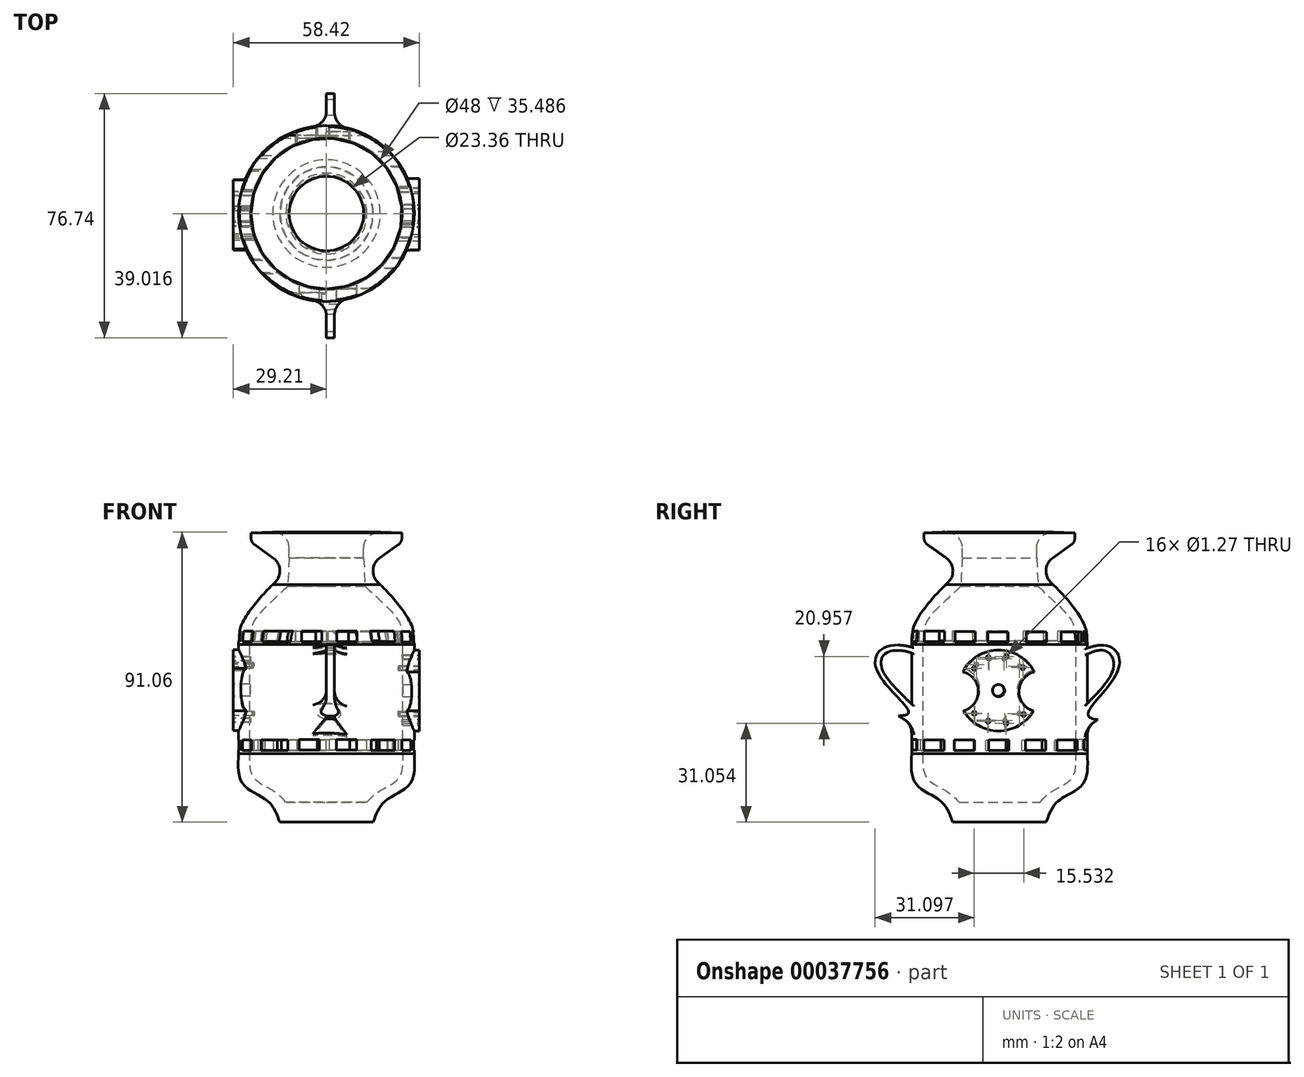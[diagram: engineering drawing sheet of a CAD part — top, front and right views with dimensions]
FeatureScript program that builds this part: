
annotation { "Feature Type Name" : "Feature", "Feature Type Description" : "" }
export const myFeature = defineFeature(function(context is Context, id is Id, definition is map)
    precondition{}
    {
        {
            var Q0;
            Q0=qCreatedBy(makeId("Right.planeOp"),FACE);
            var sketch = newSketch(context, id + "F0", { "sketchPlane" : qUnion([Q0])});
            skLineSegment(sketch, "E0", {"start": v(14.52, -21.43) * mm, "end": v(-0.17, -21.43) * mm});
            skLineSegment(sketch, "E1", {"start": v(-0.17, -21.43) * mm, "end": v(-0.17, -15.13) * mm});
            skLineSegment(sketch, "E2", {"start": v(11.5, 64.55) * mm, "end": v(11.5, 61.54) * mm});
            skLineSegment(sketch, "E3", {"start": v(-0.17, 79.99) * mm, "end": v(-0.17, -32.45) * mm, "construction": true});
            skPoint(sketch, "E4.visualSharp", {"position": v(11.5, 75.56) * mm});
            skArc(sketch, "E4.filletArc", {"start": v(16.78, 69.62) * mm, "mid": v(13.06, 68.2) * mm, "end": v(11.5, 64.55) * mm});
            skPoint(sketch, "E5.visualSharp", {"position": v(12.68, 59.63) * mm});
            skArc(sketch, "E5.filletArc", {"start": v(16.58, 61.54) * mm, "mid": v(14.44, 57.33) * mm, "end": v(16.7, 53.18) * mm});
            skPoint(sketch, "E6.visualSharp", {"position": v(11.5, 61.05) * mm});
            skArc(sketch, "E6.filletArc", {"start": v(11.5, 61.54) * mm, "mid": v(11.62, 60.46) * mm, "end": v(11.96, 59.43) * mm});
            skFitSpline(sketch, "E7", {"points": [v(16.7, 53.18) * mm, v(22.1, 47.25) * mm, v(26.83, 39.53) * mm, v(27.4, 34.38) * mm], "startDerivative": vector(15.54, -15.8) * mm, "endDerivative": vector(0.96, -17.5) * mm});
            skLineSegment(sketch, "E8", {"start": v(11.5, 61.54) * mm, "end": v(11.96, 52.7) * mm});
            skFitSpline(sketch, "E9", {"points": [v(11.96, 52.7) * mm, v(22.54, 41.67) * mm, v(23.82, 35.52) * mm], "startDerivative": vector(17.32, -18.3) * mm, "endDerivative": vector(3.54, -17.15) * mm});
            skLineSegment(sketch, "E10", {"start": v(27.4, 34.38) * mm, "end": v(27.4, 0.03) * mm});
            skLineSegment(sketch, "E11", {"start": v(23.82, 35.52) * mm, "end": v(23.82, 0.03) * mm});
            skFitSpline(sketch, "E12", {"points": [v(14.52, -21.43) * mm, v(18.24, -14.85) * mm, v(25.97, -9.55) * mm, v(27.4, 0.03) * mm], "startDerivative": vector(8.27, 23.62) * mm, "endDerivative": vector(-1.61, 31.15) * mm});
            skFitSpline(sketch, "E13", {"points": [v(23.82, 0.03) * mm, v(23.82, -3.69) * mm, v(22.25, -7.98) * mm, v(16.24, -11.84) * mm, v(12.52, -15.13) * mm], "startDerivative": vector(0.76, -16.8) * mm, "endDerivative": vector(-12.82, -13.7) * mm});
            skLineSegment(sketch, "E14", {"start": v(-0.17, -15.13) * mm, "end": v(12.52, -15.13) * mm});
            skLineSegment(sketch, "E15", {"start": v(16.78, 69.62) * mm, "end": v(23.47, 69.37) * mm});
            skLineSegment(sketch, "E16", {"start": v(16.58, 61.54) * mm, "end": v(22.41, 65.67) * mm});
            skLineSegment(sketch, "E17", {"start": v(23.48, 67.77) * mm, "end": v(23.47, 69.37) * mm});
            skPoint(sketch, "E18.visualSharp", {"position": v(23.5, 66.44) * mm});
            skArc(sketch, "E18.filletArc", {"start": v(22.41, 65.67) * mm, "mid": v(23.2, 66.59) * mm, "end": v(23.48, 67.77) * mm});
            skSolve(sketch);
        }
        {
            var Q0;
            Q0=makeQuery(id+"F0.imprint","IMPRINT",FACE,{"disambiguationData":[TD([[makeQuery(id+"F0.imprint","IMPRINT",EDGE,{"derivedFrom":sQuery(id+"F0.wireOp",EDGE,"E0")}),-1.0]])]});
            var Q1;
            Q1=sQuery(id+"F0.wireOp",EDGE,"E3");
            revolve(context, id + "F1", {"entities" : qUnion([Q0]), "axis" : qUnion([Q1]), "revolveType" : RevolveType.FULL});
        }
        {
            var Q0;
            Q0=qCreatedBy(makeId("Right.planeOp"),FACE);
            var sketch = newSketch(context, id + "F2", { "sketchPlane" : qUnion([Q0])});
            skLineSegment(sketch, "E19.bottom", {"start": v(-25.33, 38.52) * mm, "end": v(-18.98, 38.52) * mm});
            skLineSegment(sketch, "E19.top", {"start": v(-25.33, 35.22) * mm, "end": v(-18.98, 35.22) * mm});
            skLineSegment(sketch, "E19.left", {"start": v(-25.33, 38.52) * mm, "end": v(-25.33, 35.22) * mm});
            skLineSegment(sketch, "E19.right", {"start": v(-18.98, 38.52) * mm, "end": v(-18.98, 35.22) * mm});
            skLineSegment(sketch, "E20.bottom", {"start": v(-14.87, 38.52) * mm, "end": v(-8.52, 38.52) * mm});
            skLineSegment(sketch, "E20.top", {"start": v(-14.87, 35.22) * mm, "end": v(-8.52, 35.22) * mm});
            skLineSegment(sketch, "E20.left", {"start": v(-14.87, 38.52) * mm, "end": v(-14.87, 35.22) * mm});
            skLineSegment(sketch, "E20.right", {"start": v(-8.52, 38.52) * mm, "end": v(-8.52, 35.22) * mm});
            skLineSegment(sketch, "E21.bottom", {"start": v(-4.15, 38.52) * mm, "end": v(2.2, 38.52) * mm});
            skLineSegment(sketch, "E21.top", {"start": v(-4.15, 35.22) * mm, "end": v(2.2, 35.22) * mm});
            skLineSegment(sketch, "E21.left", {"start": v(-4.15, 38.52) * mm, "end": v(-4.15, 35.22) * mm});
            skLineSegment(sketch, "E21.right", {"start": v(2.2, 38.52) * mm, "end": v(2.2, 35.22) * mm});
            skLineSegment(sketch, "E22.bottom", {"start": v(7.37, 38.52) * mm, "end": v(13.72, 38.52) * mm});
            skLineSegment(sketch, "E22.top", {"start": v(7.37, 35.22) * mm, "end": v(13.72, 35.22) * mm});
            skLineSegment(sketch, "E22.left", {"start": v(7.37, 38.52) * mm, "end": v(7.37, 35.22) * mm});
            skLineSegment(sketch, "E22.right", {"start": v(13.72, 38.52) * mm, "end": v(13.72, 35.22) * mm});
            skLineSegment(sketch, "E23.bottom", {"start": v(18.1, 38.52) * mm, "end": v(24.45, 38.52) * mm});
            skLineSegment(sketch, "E23.top", {"start": v(18.1, 35.22) * mm, "end": v(24.45, 35.22) * mm});
            skLineSegment(sketch, "E23.left", {"start": v(18.1, 38.52) * mm, "end": v(18.1, 35.22) * mm});
            skLineSegment(sketch, "E23.right", {"start": v(24.45, 38.52) * mm, "end": v(24.45, 35.22) * mm});
            skLineSegment(sketch, "E24.bottom", {"start": v(-14.47, 4.36) * mm, "end": v(-8.12, 4.36) * mm});
            skLineSegment(sketch, "E24.top", {"start": v(-14.47, 1.06) * mm, "end": v(-8.12, 1.06) * mm});
            skLineSegment(sketch, "E24.left", {"start": v(-14.47, 4.36) * mm, "end": v(-14.47, 1.06) * mm});
            skLineSegment(sketch, "E24.right", {"start": v(-8.12, 4.36) * mm, "end": v(-8.12, 1.06) * mm});
            skLineSegment(sketch, "E25.bottom", {"start": v(-4.4, 4.36) * mm, "end": v(1.94, 4.36) * mm});
            skLineSegment(sketch, "E25.top", {"start": v(-4.4, 1.06) * mm, "end": v(1.94, 1.06) * mm});
            skLineSegment(sketch, "E25.left", {"start": v(-4.4, 4.36) * mm, "end": v(-4.4, 1.06) * mm});
            skLineSegment(sketch, "E25.right", {"start": v(1.94, 4.36) * mm, "end": v(1.94, 1.06) * mm});
            skLineSegment(sketch, "E26.bottom", {"start": v(6.85, 4.36) * mm, "end": v(13.2, 4.36) * mm});
            skLineSegment(sketch, "E26.top", {"start": v(6.85, 1.06) * mm, "end": v(13.2, 1.06) * mm});
            skLineSegment(sketch, "E26.left", {"start": v(6.85, 4.36) * mm, "end": v(6.85, 1.06) * mm});
            skLineSegment(sketch, "E26.right", {"start": v(13.2, 4.36) * mm, "end": v(13.2, 1.06) * mm});
            skLineSegment(sketch, "E27.bottom", {"start": v(17.18, 4.36) * mm, "end": v(23.53, 4.36) * mm});
            skLineSegment(sketch, "E27.top", {"start": v(17.18, 1.06) * mm, "end": v(23.53, 1.06) * mm});
            skLineSegment(sketch, "E27.left", {"start": v(17.18, 4.36) * mm, "end": v(17.18, 1.06) * mm});
            skLineSegment(sketch, "E27.right", {"start": v(23.53, 4.36) * mm, "end": v(23.53, 1.06) * mm});
            skLineSegment(sketch, "E28.bottom", {"start": v(-24.93, 4.36) * mm, "end": v(-18.58, 4.36) * mm});
            skLineSegment(sketch, "E28.top", {"start": v(-24.93, 1.06) * mm, "end": v(-18.58, 1.06) * mm});
            skLineSegment(sketch, "E28.left", {"start": v(-24.93, 4.36) * mm, "end": v(-24.93, 1.06) * mm});
            skLineSegment(sketch, "E28.right", {"start": v(-18.58, 4.36) * mm, "end": v(-18.58, 1.06) * mm});
            skSolve(sketch);
        }
        {
            var Q0;
            Q0 = qSketchRegion(id + "F2", true);
            extrude(context, id + "F3", {"entities" : qUnion([Q0]), "operationType" : NewBodyOperationType.REMOVE, "endBound" : BoundingType.THROUGH_ALL, "oppositeDirection" : true, "depth" : 43.48 * mm});
        }
        {
            var Q0;
            Q0=qCreatedBy(makeId("Right.planeOp"),FACE);
            var sketch = newSketch(context, id + "F4", { "sketchPlane" : qUnion([Q0])});
            skLineSegment(sketch, "E29.bottom", {"start": v(-23.72, 38.57) * mm, "end": v(-17.37, 38.57) * mm});
            skLineSegment(sketch, "E29.top", {"start": v(-23.72, 35.27) * mm, "end": v(-17.37, 35.27) * mm});
            skLineSegment(sketch, "E29.left", {"start": v(-23.72, 38.57) * mm, "end": v(-23.72, 35.27) * mm});
            skLineSegment(sketch, "E29.right", {"start": v(-17.37, 38.57) * mm, "end": v(-17.37, 35.27) * mm});
            skLineSegment(sketch, "E30.bottom", {"start": v(-14.11, 38.4) * mm, "end": v(-7.76, 38.4) * mm});
            skLineSegment(sketch, "E30.top", {"start": v(-14.11, 35.1) * mm, "end": v(-7.76, 35.1) * mm});
            skLineSegment(sketch, "E30.left", {"start": v(-14.11, 38.4) * mm, "end": v(-14.11, 35.1) * mm});
            skLineSegment(sketch, "E30.right", {"start": v(-7.76, 38.4) * mm, "end": v(-7.76, 35.1) * mm});
            skLineSegment(sketch, "E31.bottom", {"start": v(-3.76, 38.22) * mm, "end": v(2.59, 38.22) * mm});
            skLineSegment(sketch, "E31.top", {"start": v(-3.76, 34.92) * mm, "end": v(2.59, 34.92) * mm});
            skLineSegment(sketch, "E31.left", {"start": v(-3.76, 38.22) * mm, "end": v(-3.76, 34.92) * mm});
            skLineSegment(sketch, "E31.right", {"start": v(2.59, 38.22) * mm, "end": v(2.59, 34.92) * mm});
            skLineSegment(sketch, "E32.bottom", {"start": v(8.27, 38.22) * mm, "end": v(14.62, 38.22) * mm});
            skLineSegment(sketch, "E32.top", {"start": v(8.27, 34.92) * mm, "end": v(14.62, 34.92) * mm});
            skLineSegment(sketch, "E32.left", {"start": v(8.27, 38.22) * mm, "end": v(8.27, 34.92) * mm});
            skLineSegment(sketch, "E32.right", {"start": v(14.62, 38.22) * mm, "end": v(14.62, 34.92) * mm});
            skLineSegment(sketch, "E33.bottom", {"start": v(19.24, 38.22) * mm, "end": v(25.59, 38.22) * mm});
            skLineSegment(sketch, "E33.top", {"start": v(19.24, 34.92) * mm, "end": v(25.59, 34.92) * mm});
            skLineSegment(sketch, "E33.left", {"start": v(19.24, 38.22) * mm, "end": v(19.24, 34.92) * mm});
            skLineSegment(sketch, "E33.right", {"start": v(25.59, 38.22) * mm, "end": v(25.59, 34.92) * mm});
            skLineSegment(sketch, "E34.bottom", {"start": v(-23.88, 4.36) * mm, "end": v(-17.53, 4.36) * mm});
            skLineSegment(sketch, "E34.top", {"start": v(-23.88, 1.06) * mm, "end": v(-17.53, 1.06) * mm});
            skLineSegment(sketch, "E34.left", {"start": v(-23.88, 4.36) * mm, "end": v(-23.88, 1.06) * mm});
            skLineSegment(sketch, "E34.right", {"start": v(-17.53, 4.36) * mm, "end": v(-17.53, 1.06) * mm});
            skLineSegment(sketch, "E35.bottom", {"start": v(-14.34, 4.36) * mm, "end": v(-8, 4.36) * mm});
            skLineSegment(sketch, "E35.top", {"start": v(-14.34, 1.06) * mm, "end": v(-8, 1.06) * mm});
            skLineSegment(sketch, "E35.left", {"start": v(-14.34, 4.36) * mm, "end": v(-14.34, 1.06) * mm});
            skLineSegment(sketch, "E35.right", {"start": v(-8, 4.36) * mm, "end": v(-8, 1.06) * mm});
            skLineSegment(sketch, "E36.bottom", {"start": v(-3.62, 4.36) * mm, "end": v(2.73, 4.36) * mm});
            skLineSegment(sketch, "E36.top", {"start": v(-3.62, 1.06) * mm, "end": v(2.73, 1.06) * mm});
            skLineSegment(sketch, "E36.left", {"start": v(-3.62, 4.36) * mm, "end": v(-3.62, 1.06) * mm});
            skLineSegment(sketch, "E36.right", {"start": v(2.73, 4.36) * mm, "end": v(2.73, 1.06) * mm});
            skLineSegment(sketch, "E37.bottom", {"start": v(8.04, 4.36) * mm, "end": v(14.39, 4.36) * mm});
            skLineSegment(sketch, "E37.top", {"start": v(8.04, 1.06) * mm, "end": v(14.39, 1.06) * mm});
            skLineSegment(sketch, "E37.left", {"start": v(8.04, 4.36) * mm, "end": v(8.04, 1.06) * mm});
            skLineSegment(sketch, "E37.right", {"start": v(14.39, 4.36) * mm, "end": v(14.39, 1.06) * mm});
            skLineSegment(sketch, "E38.bottom", {"start": v(17.97, 4.36) * mm, "end": v(24.32, 4.36) * mm});
            skLineSegment(sketch, "E38.top", {"start": v(17.97, 1.06) * mm, "end": v(24.32, 1.06) * mm});
            skLineSegment(sketch, "E38.left", {"start": v(17.97, 4.36) * mm, "end": v(17.97, 1.06) * mm});
            skLineSegment(sketch, "E38.right", {"start": v(24.32, 4.36) * mm, "end": v(24.32, 1.06) * mm});
            skSolve(sketch);
        }
        {
            var Q0;
            Q0 = qSketchRegion(id + "F4", true);
            extrude(context, id + "F5", {"entities" : qUnion([Q0]), "operationType" : NewBodyOperationType.REMOVE, "depth" : 76.34 * mm});
        }
        {
            var Q0;
            Q0=qCreatedBy(makeId("Front.planeOp"),FACE);
            var sketch = newSketch(context, id + "F6", { "sketchPlane" : qUnion([Q0])});
            skLineSegment(sketch, "E39.bottom", {"start": v(-7.82, 38.52) * mm, "end": v(-1.47, 38.52) * mm});
            skLineSegment(sketch, "E39.top", {"start": v(-7.82, 35.22) * mm, "end": v(-1.47, 35.22) * mm});
            skLineSegment(sketch, "E39.left", {"start": v(-7.82, 38.52) * mm, "end": v(-7.82, 35.22) * mm});
            skLineSegment(sketch, "E39.right", {"start": v(-1.47, 38.52) * mm, "end": v(-1.47, 35.22) * mm});
            skLineSegment(sketch, "E40.bottom", {"start": v(3.21, 38.52) * mm, "end": v(9.56, 38.52) * mm});
            skLineSegment(sketch, "E40.top", {"start": v(3.21, 35.22) * mm, "end": v(9.56, 35.22) * mm});
            skLineSegment(sketch, "E40.left", {"start": v(3.21, 38.52) * mm, "end": v(3.21, 35.22) * mm});
            skLineSegment(sketch, "E40.right", {"start": v(9.56, 38.52) * mm, "end": v(9.56, 35.22) * mm});
            skLineSegment(sketch, "E41.bottom", {"start": v(-8.6, 4.5) * mm, "end": v(-2.26, 4.5) * mm});
            skLineSegment(sketch, "E41.top", {"start": v(-8.6, 1.2) * mm, "end": v(-2.26, 1.2) * mm});
            skLineSegment(sketch, "E41.left", {"start": v(-8.6, 4.5) * mm, "end": v(-8.6, 1.2) * mm});
            skLineSegment(sketch, "E41.right", {"start": v(-2.26, 4.5) * mm, "end": v(-2.26, 1.2) * mm});
            skLineSegment(sketch, "E42.bottom", {"start": v(3.18, 4.5) * mm, "end": v(9.53, 4.5) * mm});
            skLineSegment(sketch, "E42.top", {"start": v(3.18, 1.2) * mm, "end": v(9.53, 1.2) * mm});
            skLineSegment(sketch, "E42.left", {"start": v(3.18, 4.5) * mm, "end": v(3.18, 1.2) * mm});
            skLineSegment(sketch, "E42.right", {"start": v(9.53, 4.5) * mm, "end": v(9.53, 1.2) * mm});
            skSolve(sketch);
        }
        {
            var Q0;
            Q0=makeQuery(id+"F6.imprint","IMPRINT",FACE,{"disambiguationData":[TD([[makeQuery(id+"F6.imprint","IMPRINT",EDGE,{"derivedFrom":sQuery(id+"F6.wireOp",EDGE,"E39.bottom")}),-1.0]])]});
            var Q1;
            Q1=makeQuery(id+"F6.imprint","IMPRINT",FACE,{"disambiguationData":[TD([[makeQuery(id+"F6.imprint","IMPRINT",EDGE,{"derivedFrom":sQuery(id+"F6.wireOp",EDGE,"E40.bottom")}),-1.0]])]});
            extrude(context, id + "F7", {"entities" : qUnion([Q0, Q1]), "operationType" : NewBodyOperationType.REMOVE, "depth" : 59.65 * mm});
        }
        {
            var Q0;
            Q0=qCreatedBy(makeId("Front.planeOp"),FACE);
            var sketch = newSketch(context, id + "F8", { "sketchPlane" : qUnion([Q0])});
            skLineSegment(sketch, "E43.bottom", {"start": v(6.93, 38.44) * mm, "end": v(0.58, 38.44) * mm});
            skLineSegment(sketch, "E43.top", {"start": v(6.93, 35.14) * mm, "end": v(0.58, 35.14) * mm});
            skLineSegment(sketch, "E43.left", {"start": v(6.93, 38.44) * mm, "end": v(6.93, 35.14) * mm});
            skLineSegment(sketch, "E43.right", {"start": v(0.58, 38.44) * mm, "end": v(0.58, 35.14) * mm});
            skLineSegment(sketch, "E44.bottom", {"start": v(-3.3, 38.44) * mm, "end": v(-9.66, 38.44) * mm});
            skLineSegment(sketch, "E44.top", {"start": v(-3.3, 35.14) * mm, "end": v(-9.66, 35.14) * mm});
            skLineSegment(sketch, "E44.left", {"start": v(-3.3, 38.44) * mm, "end": v(-3.3, 35.14) * mm});
            skLineSegment(sketch, "E44.right", {"start": v(-9.66, 38.44) * mm, "end": v(-9.66, 35.14) * mm});
            skLineSegment(sketch, "E45.bottom", {"start": v(-2.79, 4.5) * mm, "end": v(-9.14, 4.5) * mm});
            skLineSegment(sketch, "E45.top", {"start": v(-2.79, 1.19) * mm, "end": v(-9.14, 1.19) * mm});
            skLineSegment(sketch, "E45.left", {"start": v(-2.79, 4.5) * mm, "end": v(-2.79, 1.19) * mm});
            skLineSegment(sketch, "E45.right", {"start": v(-9.14, 4.5) * mm, "end": v(-9.14, 1.19) * mm});
            skLineSegment(sketch, "E46.bottom", {"start": v(7.28, 4.5) * mm, "end": v(0.93, 4.5) * mm});
            skLineSegment(sketch, "E46.top", {"start": v(7.28, 1.19) * mm, "end": v(0.93, 1.19) * mm});
            skLineSegment(sketch, "E46.left", {"start": v(7.28, 4.5) * mm, "end": v(7.28, 1.19) * mm});
            skLineSegment(sketch, "E46.right", {"start": v(0.93, 4.5) * mm, "end": v(0.93, 1.19) * mm});
            skSolve(sketch);
        }
        {
            var Q0;
            Q0 = qSketchRegion(id + "F8", true);
            extrude(context, id + "F9", {"entities" : qUnion([Q0]), "operationType" : NewBodyOperationType.REMOVE, "oppositeDirection" : true, "depth" : 65.15 * mm});
        }
        {
            var Q0;
            Q0 = qSketchRegion(id + "F6", true);
            extrude(context, id + "F10", {"entities" : qUnion([Q0]), "operationType" : NewBodyOperationType.REMOVE, "depth" : 87.53 * mm});
        }
        {
            var Q0;
            Q0=qCreatedBy(makeId("Right.planeOp"),FACE);
            var sketch = newSketch(context, id + "F11", { "sketchPlane" : qUnion([Q0])});
            skArc(sketch, "E47", {"start": v(10.82, 25.72) * mm, "mid": v(-0.42, 32.54) * mm, "end": v(-11.67, 25.72) * mm});
            skArc(sketch, "E48", {"start": v(10.82, 25.72) * mm, "mid": v(5.95, 19.71) * mm, "end": v(10.53, 13.49) * mm});
            skArc(sketch, "E49", {"start": v(-11.4, 13.53) * mm, "mid": v(-6.8, 19.73) * mm, "end": v(-11.67, 25.72) * mm});
            skArc(sketch, "E50.trimOffspring", {"start": v(-11.4, 13.53) * mm, "mid": v(-0.45, 7.19) * mm, "end": v(10.53, 13.49) * mm});
            skSolve(sketch);
        }
        {
            var Q0;
            Q0 = qSketchRegion(id + "F11", true);
            extrude(context, id + "F12", {"entities" : qUnion([Q0]), "operationType" : NewBodyOperationType.ADD, "depth" : 29.2 * mm, "hasSecondDirection" : true, "secondDirectionOppositeDirection" : false, "secondDirectionDepth" : 25.17 * mm});
        }
        {
            var Q0;
            Q0=qCreatedBy(makeId("Right.planeOp"),FACE);
            var sketch = newSketch(context, id + "F13", { "sketchPlane" : qUnion([Q0])});
            skArc(sketch, "E51", {"start": v(-11.62, 13.57) * mm, "mid": v(-0.77, 7.3) * mm, "end": v(10.18, 13.38) * mm});
            skArc(sketch, "E52", {"start": v(-11.62, 13.57) * mm, "mid": v(-6.43, 20.12) * mm, "end": v(-11.33, 26.88) * mm});
            skArc(sketch, "E53", {"start": v(10.42, 26.2) * mm, "mid": v(5.46, 19.88) * mm, "end": v(10.18, 13.38) * mm});
            skArc(sketch, "E54.trimOffspring", {"start": v(10.42, 26.2) * mm, "mid": v(-0.26, 32.69) * mm, "end": v(-11.33, 26.88) * mm});
            skSolve(sketch);
        }
        {
            var Q0;
            Q0 = qSketchRegion(id + "F13", true);
            extrude(context, id + "F14", {"entities" : qUnion([Q0]), "operationType" : NewBodyOperationType.ADD, "oppositeDirection" : true, "depth" : 29.2 * mm, "hasSecondDirection" : true, "secondDirectionOppositeDirection" : true, "secondDirectionDepth" : 25.17 * mm});
        }
        {
            var Q0;
            Q0=makeQuery(id+"F14.opExtrude","CAP_FACE",FACE,{"disambiguationData":[OSD([sQuery(id+"F13.wireOp",EDGE,"E51"),sQuery(id+"F13.wireOp",EDGE,"E52"),sQuery(id+"F13.wireOp",EDGE,"E53"),sQuery(id+"F13.wireOp",EDGE,"E54.trimOffspring")])],"isStart":false});
            var sketch = newSketch(context, id + "F15", { "sketchPlane" : qUnion([Q0])});
            skCircle(sketch, "E55", {"center": v(-6.14, 27.54) * mm, "radius": 0.64 * mm});
            skCircle(sketch, "E56", {"center": v(-1.33, 29.9) * mm, "radius": 0.64 * mm});
            skCircle(sketch, "E57", {"center": v(3.4, 29.8) * mm, "radius": 0.64 * mm});
            skCircle(sketch, "E58", {"center": v(7.36, 28.01) * mm, "radius": 0.64 * mm});
            skCircle(sketch, "E59", {"center": v(7.93, 12.62) * mm, "radius": 0.64 * mm});
            skCircle(sketch, "E60", {"center": v(-6.05, 12.62) * mm, "radius": 0.64 * mm});
            skCircle(sketch, "E61", {"center": v(3.68, 10.54) * mm, "radius": 0.64 * mm});
            skCircle(sketch, "E62", {"center": v(-1.52, 10.45) * mm, "radius": 0.64 * mm});
            skCircle(sketch, "E63", {"center": v(0.66, 20) * mm, "radius": 1.9 * mm});
            skSolve(sketch);
        }
        {
            var Q0;
            Q0 = qSketchRegion(id + "F15", true);
            extrude(context, id + "F16", {"entities" : qUnion([Q0]), "operationType" : NewBodyOperationType.REMOVE, "oppositeDirection" : true, "depth" : 15.2 * mm});
        }
        {
            var Q0;
            Q0=makeQuery(id+"F12.opExtrude","CAP_FACE",FACE,{"disambiguationData":[OSD([sQuery(id+"F11.wireOp",EDGE,"E47"),sQuery(id+"F11.wireOp",EDGE,"E48"),sQuery(id+"F11.wireOp",EDGE,"E49"),sQuery(id+"F11.wireOp",EDGE,"E50.trimOffspring")])],"isStart":false});
            var sketch = newSketch(context, id + "F17", { "sketchPlane" : qUnion([Q0])});
            skCircle(sketch, "E64", {"center": v(-8.1, 26.83) * mm, "radius": 0.64 * mm});
            skCircle(sketch, "E65", {"center": v(7.19, 27.08) * mm, "radius": 0.64 * mm});
            skCircle(sketch, "E66", {"center": v(2, 30.58) * mm, "radius": 0.64 * mm});
            skCircle(sketch, "E67", {"center": v(-3.69, 30.22) * mm, "radius": 0.64 * mm});
            skCircle(sketch, "E68", {"center": v(7.44, 12.38) * mm, "radius": 0.64 * mm});
            skCircle(sketch, "E69", {"center": v(-8.1, 12.71) * mm, "radius": 0.64 * mm});
            skCircle(sketch, "E70", {"center": v(1.93, 9.62) * mm, "radius": 0.64 * mm});
            skCircle(sketch, "E71", {"center": v(-3.75, 10.2) * mm, "radius": 0.64 * mm});
            skCircle(sketch, "E72", {"center": v(-0.43, 19.86) * mm, "radius": 1.9 * mm});
            skSolve(sketch);
        }
        {
            var Q0;
            Q0 = qSketchRegion(id + "F17", true);
            extrude(context, id + "F18", {"entities" : qUnion([Q0]), "operationType" : NewBodyOperationType.REMOVE, "oppositeDirection" : true, "depth" : 39.9 * mm});
        }
        {
            var Q0;
            Q0=qCreatedBy(makeId("Right.planeOp"),FACE);
            var sketch = newSketch(context, id + "F19", { "sketchPlane" : qUnion([Q0])});
            skFitSpline(sketch, "E73", {"points": [v(27.24, 33.1) * mm, v(37.43, 27.67) * mm, v(27.63, 12.7) * mm, v(30.68, 10.72) * mm], "startDerivative": vector(61.07, 24.57) * mm, "endDerivative": vector(27.38, -3.3) * mm});
            skFitSpline(sketch, "E74", {"points": [v(27.14, 31.23) * mm, v(33.2, 32.3) * mm, v(35.71, 27.54) * mm, v(27.24, 15.62) * mm], "startDerivative": vector(21.7, 9.6) * mm, "endDerivative": vector(-27.3, -27.9) * mm});
            skFitSpline(sketch, "E75", {"points": [v(30.68, 10.72) * mm, v(27.24, 8.47) * mm], "startDerivative": vector(-3.44, -2.25) * mm, "endDerivative": vector(-3.44, -2.25) * mm});
            skLineSegment(sketch, "E76", {"start": v(27.24, 15.62) * mm, "end": v(27.24, 8.47) * mm});
            skLineSegment(sketch, "E77", {"start": v(27.14, 31.23) * mm, "end": v(27.24, 33.1) * mm});
            skLineSegment(sketch, "E78", {"start": v(-0.17, 69.37) * mm, "end": v(-0.17, -25.05) * mm, "construction": true});
            skSolve(sketch);
        }
        {
            var Q0;
            Q0 = qSketchRegion(id + "F19", true);
            extrude(context, id + "F20", {"entities" : qUnion([Q0]), "operationType" : NewBodyOperationType.ADD, "depth" : 2.54 * mm});
        }
        {
            var Q0;
            Q0=makeQuery(id+"F20.boolean.opBoolean","INTERSECT",EDGE,{"disambiguationData":[OD(0.0)],"derivedFrom":[makeQuery(id+"F1.opRevolve","SWEPT_FACE",FACE,{"disambiguationData":[OSD([sQuery(id+"F0.wireOp",EDGE,"E10")])]}),makeQuery(id+"F20.opExtrude","CAP_FACE",FACE,{"disambiguationData":[OSD([sQuery(id+"F19.wireOp",EDGE,"E73"),sQuery(id+"F19.wireOp",EDGE,"E74"),sQuery(id+"F19.wireOp",EDGE,"E75"),sQuery(id+"F19.wireOp",EDGE,"E76"),sQuery(id+"F19.wireOp",EDGE,"E77")])],"isStart":false})]});
            var Q1;
            Q1=makeQuery(id+"F20.boolean.opBoolean","INTERSECT",EDGE,{"disambiguationData":[OD(0.0)],"derivedFrom":[makeQuery(id+"F1.opRevolve","SWEPT_FACE",FACE,{"disambiguationData":[OSD([sQuery(id+"F0.wireOp",EDGE,"E10")])]}),makeQuery(id+"F20.opExtrude","CAP_FACE",FACE,{"disambiguationData":[OSD([sQuery(id+"F19.wireOp",EDGE,"E73"),sQuery(id+"F19.wireOp",EDGE,"E74"),sQuery(id+"F19.wireOp",EDGE,"E75"),sQuery(id+"F19.wireOp",EDGE,"E76"),sQuery(id+"F19.wireOp",EDGE,"E77")])],"isStart":true})]});
            var Q2;
            Q2=makeQuery(id+"F20.boolean.opBoolean","INTERSECT",EDGE,{"derivedFrom":[makeQuery(id+"F1.opRevolve","SWEPT_FACE",FACE,{"disambiguationData":[OSD([sQuery(id+"F0.wireOp",EDGE,"E10")])]}),makeQuery(id+"F20.opExtrude","SWEPT_FACE",FACE,{"disambiguationData":[OSD([sQuery(id+"F19.wireOp",EDGE,"E75")])]})]});
            fillet(context, id + "F21", {"entities" : qUnion([Q0, Q1, Q2]), "radius" : 5.08 * mm, "tangentPropagation" : true, "allowEdgeOverflow" : false});
        }
        {
            var Q0;
            Q0=qCreatedBy(makeId("Right.planeOp"),FACE);
            var sketch = newSketch(context, id + "F22", { "sketchPlane" : qUnion([Q0])});
            skFitSpline(sketch, "E79.MirrorCS", {"points": [v(-27.43, 31.53) * mm, v(-35.54, 31.78) * mm, v(-37.12, 27.03) * mm, v(-26.92, 14.9) * mm], "startDerivative": vector(-22.38, 10.1) * mm, "endDerivative": vector(27.57, -25.82) * mm});
            skFitSpline(sketch, "E80.MirrorCS", {"points": [v(-27.48, 33.4) * mm, v(-38.99, 27.28) * mm, v(-28.66, 13.24) * mm, v(-31.83, 11.91) * mm], "startDerivative": vector(-68.44, 20) * mm, "endDerivative": vector(-27.52, -1.8) * mm});
            skFitSpline(sketch, "E81.MirrorCS", {"points": [v(-31.83, 11.91) * mm, v(-27.59, 9.31) * mm], "startDerivative": vector(3.32, -2.44) * mm, "endDerivative": vector(3.32, -2.44) * mm});
            skLineSegment(sketch, "E82.MirrorCS", {"start": v(-27.43, 31.53) * mm, "end": v(-27.48, 33.4) * mm});
            skLineSegment(sketch, "E83", {"start": v(-26.92, 14.9) * mm, "end": v(-27.59, 9.31) * mm});
            skSolve(sketch);
        }
        {
            var Q0;
            Q0 = qSketchRegion(id + "F22", true);
            extrude(context, id + "F23", {"entities" : qUnion([Q0]), "operationType" : NewBodyOperationType.ADD, "depth" : 2.54 * mm});
        }
        {
            var Q0;
            Q0=makeQuery(id+"F23.boolean.opBoolean","INTERSECT",EDGE,{"derivedFrom":[makeQuery(id+"F1.opRevolve","SWEPT_FACE",FACE,{"disambiguationData":[OSD([sQuery(id+"F0.wireOp",EDGE,"E10")])]}),makeQuery(id+"F23.opExtrude","SWEPT_FACE",FACE,{"disambiguationData":[OSD([sQuery(id+"F22.wireOp",EDGE,"E81.MirrorCS")])]})]});
            var Q1;
            Q1=makeQuery(id+"F23.boolean.opBoolean","INTERSECT",EDGE,{"disambiguationData":[OD(0.0)],"derivedFrom":[makeQuery(id+"F1.opRevolve","SWEPT_FACE",FACE,{"disambiguationData":[OSD([sQuery(id+"F0.wireOp",EDGE,"E10")])]}),makeQuery(id+"F23.opExtrude","CAP_FACE",FACE,{"disambiguationData":[OSD([sQuery(id+"F22.wireOp",EDGE,"E79.MirrorCS"),sQuery(id+"F22.wireOp",EDGE,"E80.MirrorCS"),sQuery(id+"F22.wireOp",EDGE,"E81.MirrorCS"),sQuery(id+"F22.wireOp",EDGE,"E82.MirrorCS"),sQuery(id+"F22.wireOp",EDGE,"E83")])],"isStart":true})]});
            var Q2;
            Q2=makeQuery(id+"F23.boolean.opBoolean","INTERSECT",EDGE,{"disambiguationData":[OD(0.0)],"derivedFrom":[makeQuery(id+"F1.opRevolve","SWEPT_FACE",FACE,{"disambiguationData":[OSD([sQuery(id+"F0.wireOp",EDGE,"E10")])]}),makeQuery(id+"F23.opExtrude","CAP_FACE",FACE,{"disambiguationData":[OSD([sQuery(id+"F22.wireOp",EDGE,"E79.MirrorCS"),sQuery(id+"F22.wireOp",EDGE,"E80.MirrorCS"),sQuery(id+"F22.wireOp",EDGE,"E81.MirrorCS"),sQuery(id+"F22.wireOp",EDGE,"E82.MirrorCS"),sQuery(id+"F22.wireOp",EDGE,"E83")])],"isStart":false})]});
            fillet(context, id + "F24", {"entities" : qUnion([Q0, Q1, Q2]), "radius" : 5.08 * mm, "tangentPropagation" : true, "allowEdgeOverflow" : false});
        }
    });
